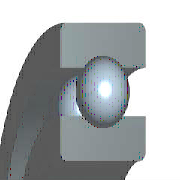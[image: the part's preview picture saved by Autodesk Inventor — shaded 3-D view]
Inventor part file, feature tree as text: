
AUTODESK INVENTOR PART (.ipt)
format: ipt  version: 2025 (Build 290162000, 162)  size: 265,728 bytes
history: native  units: mm (DEFAULTED — no unit token found)
features: other x1, pattern_circular x1
ambient origin geometry x8: Origin, YZ Plane, XZ Plane, XY Plane, X Axis, Y Axis, Z Axis, Center Point
bodies: Solid1 (feature_tree)
feature tree (2):
  other  "轴承体"
  pattern_circular  "IDS_ARRAYBALL[SIMPL:T]"  Angle=90.0deg  [1 undecoded]
note: 1 required parameter value undecoded (feature->parameter linkage not recoverable at this tier; creation-order binding heuristic only, values carry confidence <= 0.55)
